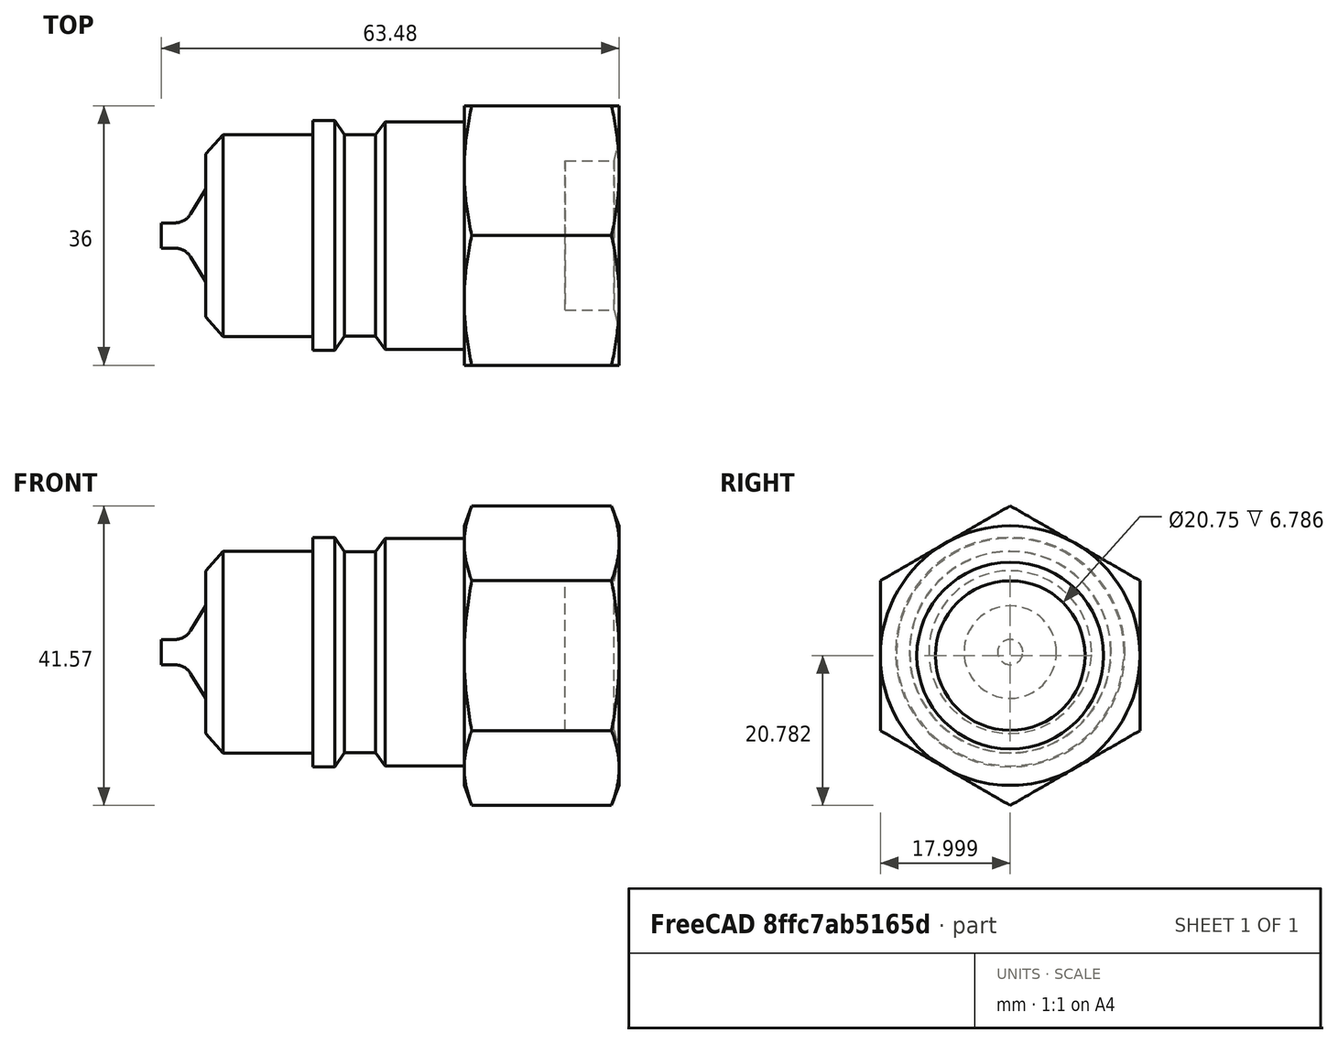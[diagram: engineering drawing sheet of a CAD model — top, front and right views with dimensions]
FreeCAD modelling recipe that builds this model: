
FCSTD DOCUMENT  (FreeCAD 0.16R6706 (Git))
Label: 3_4_quick coupler Male
License: All rights reserved
LicenseURL: http://en.wikipedia.org/wiki/All_rights_reserved
objects: App::MeasureDistance×2, Sketcher::SketchObject×1, PartDesign::Revolution×1, Part::FeaturePython×1, Part::MultiFuse×1
note: 5 computed .brp shape members not serialized (recipe doc carries the construction recipe); baked Part::Feature solids carry a one-line shape summary decoded from their .brp

FEATURE [Sketcher::SketchObject] Sketch
  Placement = pos=(0,0,0) rot=(-1,0,0;4.71239rad)
  sketch-geometry (30):
    g0: LineSegment StartX=-42.8542 StartY=-11.2837 StartZ=0 EndX=-40.4667 EndY=-14 EndZ=0
    g1: LineSegment StartX=-28 StartY=-14 StartZ=0 EndX=-40.4667 EndY=-14 EndZ=0
    g2: LineSegment StartX=-28 StartY=-14 StartZ=0 EndX=-28 EndY=-15.9239 EndZ=0
    g3: LineSegment StartX=-28 StartY=-15.9239 StartZ=0 EndX=-24.9718 EndY=-15.9239 EndZ=0
    g4: LineSegment StartX=-24.9718 StartY=-15.9239 StartZ=0 EndX=-23.6546 EndY=-13.9506 EndZ=0
    g5: LineSegment StartX=-23.6546 StartY=-13.9506 StartZ=0 EndX=-19.3015 EndY=-13.9506 EndZ=0
    g6: LineSegment StartX=-19.3015 StartY=-13.9506 StartZ=0 EndX=-17.9936 EndY=-15.778 EndZ=0
    g7: LineSegment StartX=-17.9936 StartY=-15.778 StartZ=0 EndX=-6.21328 EndY=-15.778 EndZ=0
    g8: LineSegment StartX=-6.21328 StartY=-15.778 StartZ=0 EndX=-6.21328 EndY=-17.5332 EndZ=0
    g9: LineSegment StartX=-6.21328 StartY=-17.5332 StartZ=0 EndX=7 EndY=-17.5332 EndZ=0
    g10: LineSegment StartX=-42.8542 StartY=-11.2837 StartZ=0 EndX=-42.8736 EndY=-6.40644 EndZ=0
    g11: LineSegment StartX=7 StartY=-17.5332 StartZ=0 EndX=7 EndY=0 EndZ=0
    g12: LineSegment StartX=-42 StartY=0 StartZ=0 EndX=7 EndY=0 EndZ=0
    g13: LineSegment [constr] StartX=-51.0617 StartY=-2.99968 StartZ=0 EndX=-47.2274 EndY=-2.99968 EndZ=0
    g14: LineSegment [constr] StartX=-47.2274 StartY=-2.99968 StartZ=0 EndX=-47.2274 EndY=-17.4997 EndZ=0
    g15: LineSegment [constr] StartX=-47.2274 StartY=-17.4997 StartZ=0 EndX=-51.0617 EndY=-17.4997 EndZ=0
    g16: LineSegment [constr] StartX=-51.0617 StartY=-17.4997 StartZ=0 EndX=-51.0617 EndY=-2.99968 EndZ=0
    g17: LineSegment [constr] StartX=-42.9595 StartY=9.80413 StartZ=0 EndX=14.0405 EndY=9.80413 EndZ=0
    g18: LineSegment [constr] StartX=14.0405 StartY=9.80413 StartZ=0 EndX=14.0405 EndY=-8.28035 EndZ=0
    g19: LineSegment [constr] StartX=14.0405 StartY=-8.28035 StartZ=0 EndX=-42.9595 EndY=-8.28035 EndZ=0
    g20: LineSegment [constr] StartX=-42.9595 StartY=-8.28035 StartZ=0 EndX=-42.9595 EndY=9.80413 EndZ=0
    g21: LineSegment [constr] StartX=-11.3091 StartY=-0.06637 StartZ=0 EndX=7 EndY=-0.06637 EndZ=0
    g22: LineSegment [constr] StartX=7 StartY=-0.06637 StartZ=0 EndX=7 EndY=-17.5664 EndZ=0
    g23: LineSegment [constr] StartX=7 StartY=-17.5664 StartZ=0 EndX=-11.3091 EndY=-17.5664 EndZ=0
    g24: LineSegment [constr] StartX=-11.3091 StartY=-17.5664 StartZ=0 EndX=-11.3091 EndY=-0.06637 EndZ=0
    g25: LineSegment StartX=-42.8736 StartY=-6.40644 StartZ=0 EndX=-44.9433 EndY=-3.00657 EndZ=0
    g26: LineSegment StartX=-47.1883 StartY=-1.74499 StartZ=0 EndX=-49 EndY=-1.74499 EndZ=0
    g27: ArcOfCircle CenterX=-47.1883 CenterY=-4.37323 CenterZ=0 NormalX=0 NormalY=0 NormalZ=1 Radius=2.62824 StartAngle=0.546842 EndAngle=1.5708
    g28: LineSegment StartX=-49 StartY=-1.74499 StartZ=0 EndX=-49 EndY=0 EndZ=0
    g29: LineSegment StartX=-42 StartY=0 StartZ=0 EndX=-49 EndY=0 EndZ=0
  constraints (58):
    c: Horizontal(g1)
    c: Coincident(g2,g1)
    c: Vertical(g2)
    c: Coincident(g2,g3)
    c: Horizontal(g3)
    c: Coincident(g3,g4)
    c: Coincident(g4,g5)
    c: Horizontal(g5)
    c: Coincident(g5,g6)
    c: Coincident(g6,g7)
    c: Horizontal(g7)
    c: Coincident(g7,g8)
    c: Vertical(g8)
    c: Coincident(g8,g9)
    c: Horizontal(g9)
    c: Coincident(g10,g0)
    c: Coincident(g0,g1)
    c: Vertical(g11)
    c: Coincident(g9,g11)
    c: Coincident(g12,g11)
    c: Horizontal(g12)
    c: Coincident(g13,g14)
    c: Coincident(g14,g15)
    c: Coincident(g15,g16)
    c: Coincident(g16,g13)
    c: Horizontal(g13)
    c: Horizontal(g15)
    c: Vertical(g14)
    c: Vertical(g16)
    c: Distance(g16) = 14.5
    c: Coincident(g17,g18)
    c: Coincident(g18,g19)
    c: Coincident(g19,g20)
    c: Coincident(g20,g17)
    c: Horizontal(g17)
    c: Horizontal(g19)
    c: Vertical(g18)
    c: Vertical(g20)
    c: Distance(g17) = 57
    c: Coincident(g21,g22)
    c: Coincident(g22,g23)
    c: Coincident(g23,g24)
    c: Coincident(g24,g21)
    c: Horizontal(g21)
    c: Horizontal(g23)
    c: Vertical(g22)
    c: Vertical(g24)
    c: Distance(g22) = 17.5
    c: Horizontal(g26)
    c: Tangent(g25,g27) = -1.5708
    c: Tangent(g26,g27) = -1.5708
    c: Coincident(g10,g25)
    c: Coincident(g28,g26)
    c: PointOnObject(g28,g-1)
    c: Vertical(g28)
    c: Coincident(g29,g12)
    c: Coincident(g29,g28)
    c: Horizontal(g29)
FEATURE [PartDesign::Revolution] Revolution
  Angle = 360
  Axis = (1,0,0)
  Base = (0,0,0)
  Placement = pos=(0,0,0) rot=(-1,0,0;4.71239rad)
  ReferenceAxis = -> Sketch [H_Axis]
  Sketch = -> Sketch
FEATURE [Part::FeaturePython] Nut  label="M24-Nut"  # Fasteners workbench fastener (typed FeaturePython)
  Placement = pos=(-7.02471,-0.000798049,-0.488304) rot=(0,1,0;1.5708rad)
  diameter = 17
  invert = false
  matchOuter = false
  offset = 0
  thread = false
  type = 1
FEATURE [Part::MultiFuse] Fusion
  Shapes = -> [Nut,Revolution]
FEATURE [App::MeasureDistance] Distance  label="Distance: 65.1445 mm"
  Distance = 65.1445
  P1 = (-49,-1.34454,1.1123)
  P2 = (14.4307,6.78607,-11.3073)
FEATURE [App::MeasureDistance] Distance001  label="Distance: 57.5551 mm"
  Distance = 57.5551
  P1 = (-42.8542,-0.64006,11.1947)
  P2 = (14.4753,4.42836,11.6807)
